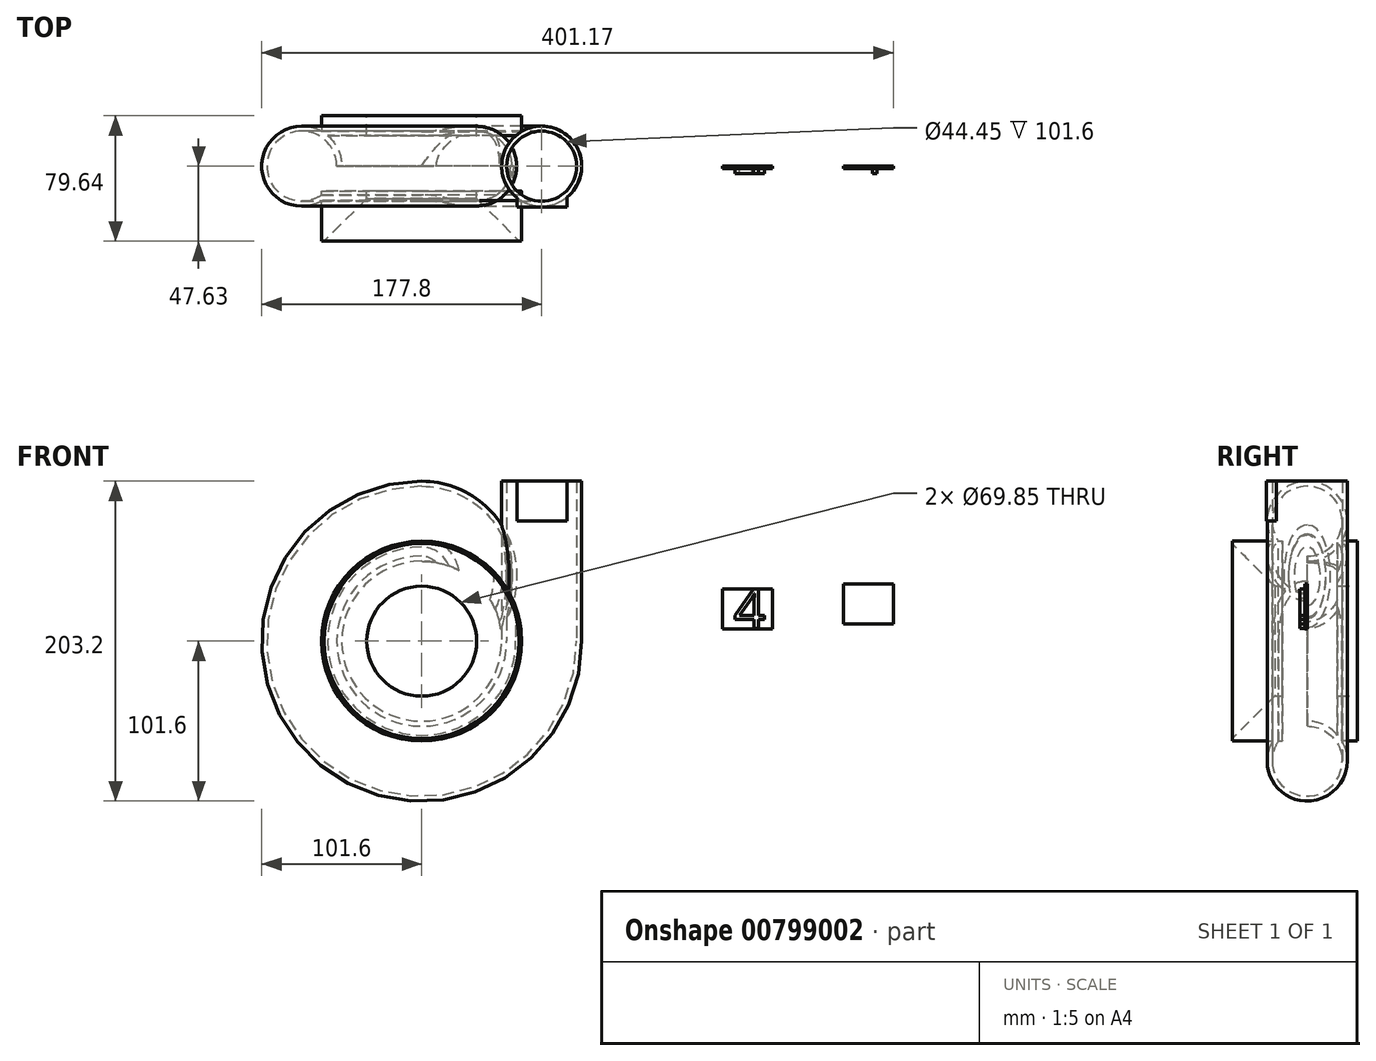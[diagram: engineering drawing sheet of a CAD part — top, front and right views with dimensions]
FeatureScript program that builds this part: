
annotation { "Feature Type Name" : "Feature", "Feature Type Description" : "" }
export const myFeature = defineFeature(function(context is Context, id is Id, definition is map)
    precondition{}
    {
        {
            var Q0;
            Q0=qCreatedBy(makeId("Front.planeOp"),FACE);
            var sketch = newSketch(context, id + "F0", { "sketchPlane" : qUnion([Q0])});
            skCircle(sketch, "E0", {"center": v(0, 0) * mm, "radius": 38.1 * mm});
            skCircle(sketch, "E1", {"center": v(0, 0) * mm, "radius": 50.8 * mm});
            skLineSegment(sketch, "E2.bottom", {"start": v(222.87, 7.67) * mm, "end": v(191.12, 7.67) * mm});
            skLineSegment(sketch, "E2.top", {"start": v(222.87, 33.07) * mm, "end": v(191.12, 33.07) * mm});
            skLineSegment(sketch, "E2.left", {"start": v(222.87, 7.67) * mm, "end": v(222.87, 33.07) * mm});
            skLineSegment(sketch, "E2.right", {"start": v(191.12, 7.67) * mm, "end": v(191.12, 33.07) * mm});
            skPoint(sketch, "E2.middle", {"position": v(207, 20.37) * mm});
            skLineSegment(sketch, "E3.bottom", {"start": v(299.57, 11.1) * mm, "end": v(267.82, 11.1) * mm});
            skLineSegment(sketch, "E3.top", {"start": v(299.57, 36.5) * mm, "end": v(267.82, 36.5) * mm});
            skLineSegment(sketch, "E3.left", {"start": v(299.57, 11.1) * mm, "end": v(299.57, 36.5) * mm});
            skLineSegment(sketch, "E3.right", {"start": v(267.82, 11.1) * mm, "end": v(267.82, 36.5) * mm});
            skPoint(sketch, "E3.middle", {"position": v(283.7, 23.8) * mm});
            skSolve(sketch);
        }
        {
            var Q0;
            Q0=qCreatedBy(makeId("Right.planeOp"),FACE);
            var sketch = newSketch(context, id + "F1", { "sketchPlane" : qUnion([Q0])});
            skCircle(sketch, "E4", {"center": v(0, 76.2) * mm, "radius": 25.4 * mm});
            skCircle(sketch, "E5", {"center": v(0, 76.2) * mm, "radius": 22.23 * mm});
            skSolve(sketch);
        }
        {
            var Q0;
            Q0=makeQuery(id+"F1.imprint","IMPRINT",FACE,{"disambiguationData":[TD([[makeQuery(id+"F1.imprint","IMPRINT",EDGE,{"derivedFrom":sQuery(id+"F1.wireOp",EDGE,"E4")}),1.0]])]});
            var Q1;
            Q1=sQuery(id+"F0.wireOp",EDGE,"E1");
            revolve(context, id + "F2", {"surfaceOperationType" : NewSurfaceOperationType.NEW, "entities" : qUnion([Q0]), "axis" : qUnion([Q1]), "revolveType" : RevolveType.ONE_DIRECTION, "angle" : 270 * degree});
        }
        {
            var Q0;
            Q0=makeQuery(id+"F2.opRevolve","CAP_FACE",FACE,{"disambiguationData":[OSD([sQuery(id+"F1.wireOp",EDGE,"E4"),sQuery(id+"F1.wireOp",EDGE,"E5")])],"isStart":false});
            extrude(context, id + "F3", {"entities" : qUnion([Q0]), "operationType" : NewBodyOperationType.ADD, "depth" : 101.6 * mm, "offsetDistance" : 25.4 * mm});
        }
        {
            var Q0;
            Q0=qCreatedBy(makeId("Front.planeOp"),FACE);
            var sketch = newSketch(context, id + "F4", { "sketchPlane" : qUnion([Q0])});
            skCircle(sketch, "E6", {"center": v(0, 41.28) * mm, "radius": 9.53 * mm, "construction": true});
            skSolve(sketch);
        }
        {
            var Q0;
            Q0=makeQuery(id+"F1.imprint","IMPRINT",FACE,{"disambiguationData":[TD([[makeQuery(id+"F1.imprint","IMPRINT",EDGE,{"derivedFrom":sQuery(id+"F1.wireOp",EDGE,"E4")}),1.0]])]});
            var Q1;
            Q1=sQuery(id+"F4.wireOp",EDGE,"E6");
            revolve(context, id + "F5", {"operationType" : NewBodyOperationType.ADD, "surfaceOperationType" : NewSurfaceOperationType.NEW, "entities" : qUnion([Q0]), "axis" : qUnion([Q1]), "revolveType" : RevolveType.ONE_DIRECTION, "oppositeDirection" : true, "angle" : 129.12 * degree});
        }
        {
            var Q0;
            Q0=sQuery(id+"F0.wireOp",VERTEX,"E1.center");
            var Q1;
            Q1=makeQuery(id+"F2.opRevolve","SWEPT_BODY",BODY,{"disambiguationData":[OSD([sQuery(id+"F1.wireOp",EDGE,"E4"),sQuery(id+"F1.wireOp",EDGE,"E5")])]});
            hole(context, id + "F6", {"style" : HoleStyle.SIMPLE, "endStyle" : HoleEndStyle.THROUGH, "holeDiameter" : 101.6 * mm, "majorDiameter" : 6.35 * mm, "isTappedThrough" : true, "tappedDepth" : 12.7 * mm, "tapClearance" : 3, "locations" : qUnion([Q0]), "scope" : qUnion([Q1]), "startStyle" : HoleStartStyle.PART});
        }
        {
            var Q0;
            Q0=sQuery(id+"F0.wireOp",VERTEX,"E1.center");
            var Q1;
            Q1=makeQuery(id+"F2.opRevolve","SWEPT_BODY",BODY,{"disambiguationData":[OSD([sQuery(id+"F1.wireOp",EDGE,"E4"),sQuery(id+"F1.wireOp",EDGE,"E5")])]});
            hole(context, id + "F7", {"style" : HoleStyle.SIMPLE, "endStyle" : HoleEndStyle.THROUGH, "oppositeDirection" : true, "holeDiameter" : 127 * mm, "majorDiameter" : 6.35 * mm, "isTappedThrough" : true, "tappedDepth" : 12.7 * mm, "tapClearance" : 3, "locations" : qUnion([Q0]), "scope" : qUnion([Q1]), "startStyle" : HoleStartStyle.PART});
        }
        {
            var Q0;
            Q0=makeQuery(id+"F0.imprint","IMPRINT",FACE,{"disambiguationData":[TD([[makeQuery(id+"F0.imprint","IMPRINT",EDGE,{"derivedFrom":sQuery(id+"F0.wireOp",EDGE,"E0")}),1.0]])]});
            cPlane(context, id + "F8", {"entities" : qUnion([Q0]), "cplaneType" : CPlaneType.OFFSET, "offset" : 15.88 * mm, "width" : 152.4 * mm, "height" : 152.4 * mm});
        }
        {
            var Q0;
            Q0=qCreatedBy(id+"F8.planeOp",FACE);
            var sketch = newSketch(context, id + "F9", { "sketchPlane" : qUnion([Q0])});
            skCircle(sketch, "E7", {"center": v(0, 0) * mm, "radius": 63.5 * mm});
            skSolve(sketch);
        }
        {
            var Q0;
            Q0=makeQuery(id+"F9.imprint","IMPRINT",FACE,{"disambiguationData":[TD([[makeQuery(id+"F9.imprint","IMPRINT",EDGE,{"derivedFrom":sQuery(id+"F9.wireOp",EDGE,"E7")}),1.0]])]});
            extrude(context, id + "F10", {"entities" : qUnion([Q0]), "operationType" : NewBodyOperationType.ADD, "depth" : 31.75 * mm, "offsetDistance" : 25.4 * mm});
        }
        {
            var Q0;
            Q0=makeQuery(id+"F0.imprint","IMPRINT",FACE,{"disambiguationData":[TD([[makeQuery(id+"F0.imprint","IMPRINT",EDGE,{"derivedFrom":sQuery(id+"F0.wireOp",EDGE,"E0")}),-1.0]])]});
            cPlane(context, id + "F11", {"entities" : qUnion([Q0]), "cplaneType" : CPlaneType.OFFSET, "offset" : 19.3 * mm, "oppositeDirection" : true, "width" : 152.4 * mm, "height" : 152.4 * mm});
        }
        {
            var Q0;
            Q0=qCreatedBy(id+"F11.planeOp",FACE);
            var sketch = newSketch(context, id + "F12", { "sketchPlane" : qUnion([Q0])});
            skCircle(sketch, "E8", {"center": v(0, 0) * mm, "radius": 63.5 * mm});
            skSolve(sketch);
        }
        {
            var Q0;
            Q0=makeQuery(id+"F12.imprint","IMPRINT",FACE,{"disambiguationData":[TD([[makeQuery(id+"F12.imprint","IMPRINT",EDGE,{"derivedFrom":sQuery(id+"F12.wireOp",EDGE,"E8")}),1.0]])]});
            extrude(context, id + "F13", {"entities" : qUnion([Q0]), "operationType" : NewBodyOperationType.ADD, "oppositeDirection" : true, "depth" : 12.7 * mm, "offsetDistance" : 25.4 * mm});
        }
        {
            var Q0;
            Q0=makeQuery(id+"F10.opExtrude","CAP_FACE",FACE,{"disambiguationData":[OSD([sQuery(id+"F9.wireOp",EDGE,"E7")])],"isStart":false});
            var sketch = newSketch(context, id + "F14", { "sketchPlane" : qUnion([Q0])});
            skPoint(sketch, "E9", {"position": v(0, 0) * mm});
            skSolve(sketch);
        }
        {
            var Q0;
            Q0=sQuery(id+"F14.wireOp",VERTEX,"E9");
            var Q1;
            Q1=makeQuery(id+"F2.opRevolve","SWEPT_BODY",BODY,{"disambiguationData":[OSD([sQuery(id+"F1.wireOp",EDGE,"E4"),sQuery(id+"F1.wireOp",EDGE,"E5")])]});
            hole(context, id + "F15", {"style" : HoleStyle.C_SINK, "endStyle" : HoleEndStyle.THROUGH, "holeDiameter" : 69.85 * mm, "cSinkDiameter" : 123.82 * mm, "cSinkAngle" : 90 * degree, "majorDiameter" : 6.35 * mm, "isTappedThrough" : true, "tappedDepth" : 12.7 * mm, "tapClearance" : 3, "locations" : qUnion([Q0]), "scope" : qUnion([Q1]), "startStyle" : HoleStartStyle.PART});
        }
        {
            var Q0;
            Q0=makeQuery(id+"F3.opExtrude","CAP_FACE",FACE,{"disambiguationData":[OSD([sQuery(id+"F1.wireOp",EDGE,"E4"),sQuery(id+"F1.wireOp",EDGE,"E5")])],"isStart":false});
            cPlane(context, id + "F16", {"entities" : qUnion([Q0]), "cplaneType" : CPlaneType.OFFSET, "offset" : 0 * mm, "width" : 152.4 * mm, "height" : 152.4 * mm});
        }
        {
            var Q0;
            Q0=qCreatedBy(id+"F16.planeOp",FACE);
            var sketch = newSketch(context, id + "F17", { "sketchPlane" : qUnion([Q0])});
            skLineSegment(sketch, "E10.bottom", {"start": v(92.23, -25.89) * mm, "end": v(60.48, -25.89) * mm});
            skLineSegment(sketch, "E10.top", {"start": v(92.23, -18.32) * mm, "end": v(60.48, -18.32) * mm});
            skLineSegment(sketch, "E10.left", {"start": v(92.23, -25.89) * mm, "end": v(92.23, -18.32) * mm});
            skLineSegment(sketch, "E10.right", {"start": v(60.48, -25.89) * mm, "end": v(60.48, -18.32) * mm});
            skPoint(sketch, "E10.middle", {"position": v(76.36, -22.1) * mm});
            skCircle(sketch, "E11", {"center": v(76.09, -0.08) * mm, "radius": 25.25 * mm});
            skSolve(sketch);
        }
        {
            var Q0;
            {var subQ0=sQuery(id+"F17.wireOp",EDGE,"E10.bottom");Q0=makeQuery(id+"F17.imprint","IMPRINT",FACE,{"disambiguationData":[TD([[makeQuery(id+"F17.imprint","IMPRINT",EDGE,{"derivedFrom":subQ0}),-1.0]])]});}
            extrude(context, id + "F18", {"entities" : qUnion([Q0]), "operationType" : NewBodyOperationType.ADD, "oppositeDirection" : true, "depth" : 25.4 * mm, "offsetDistance" : 25.4 * mm});
        }
        {
            var Q0;
            Q0=makeQuery(id+"F0.imprint","IMPRINT",FACE,{"disambiguationData":[TD([[makeQuery(id+"F0.imprint","IMPRINT",EDGE,{"derivedFrom":sQuery(id+"F0.wireOp",EDGE,"E2.bottom")}),-1.0]])]});
            extrude(context, id + "F19", {"entities" : qUnion([Q0]), "depth" : 1.59 * mm, "offsetDistance" : 25.4 * mm});
        }
        {
            var Q0;
            Q0=makeQuery(id+"F0.imprint","IMPRINT",FACE,{"disambiguationData":[TD([[makeQuery(id+"F0.imprint","IMPRINT",EDGE,{"derivedFrom":sQuery(id+"F0.wireOp",EDGE,"E3.bottom")}),-1.0]])]});
            extrude(context, id + "F20", {"entities" : qUnion([Q0]), "depth" : 1.59 * mm, "offsetDistance" : 25.4 * mm});
        }
        {
            var Q0;
            Q0=makeQuery(id+"F20.opExtrude","CAP_FACE",FACE,{"disambiguationData":[OSD([sQuery(id+"F0.wireOp",EDGE,"E3.bottom"),sQuery(id+"F0.wireOp",EDGE,"E3.top"),sQuery(id+"F0.wireOp",EDGE,"E3.left"),sQuery(id+"F0.wireOp",EDGE,"E3.right")])],"isStart":false});
            var sketch = newSketch(context, id + "F21", { "sketchPlane" : qUnion([Q0])});
            skText(sketch, "E12", { "text": "1\n", "fontName": "OpenSans-Regular.ttf"});
            skText(sketch, "E13", { "text": "4", "fontName": "OpenSans-Regular.ttf"});
            const initialGuessF21  = {"E12": [0.2749, 0.0111, 1, 0, 0.0254], "E13": [0.19827, 0.00806, 1, 0, 0.02516]};
            skSetInitialGuess(sketch, initialGuessF21);
            skSolve(sketch);
        }
        {
            var Q0;
            Q0=makeQuery(id+"F21.imprint","IMPRINT",FACE,{"disambiguationData":[TD([[makeQuery(id+"F21.imprint","IMPRINT",EDGE,{"derivedFrom":sQuery(id+"F21.wireOp",EDGE,"E13.sketch_text.stroke-0")}),-1.0]])]});
            extrude(context, id + "F22", {"entities" : qUnion([Q0]), "operationType" : NewBodyOperationType.ADD, "depth" : 3.17 * mm, "offsetDistance" : 25.4 * mm});
        }
        {
            var Q0;
            Q0=makeQuery(id+"F20.opExtrude","CAP_FACE",FACE,{"disambiguationData":[OSD([sQuery(id+"F0.wireOp",EDGE,"E3.bottom"),sQuery(id+"F0.wireOp",EDGE,"E3.top"),sQuery(id+"F0.wireOp",EDGE,"E3.left"),sQuery(id+"F0.wireOp",EDGE,"E3.right")])],"isStart":false});
            var sketch = newSketch(context, id + "F23", { "sketchPlane" : qUnion([Q0])});
            skText(sketch, "E14", { "text": "1", "fontName": "OpenSans-Regular.ttf"});
            const initialGuessF23  = {"E14": [0.2767, 0.0111, 1, 0, 0.0254]};
            skSetInitialGuess(sketch, initialGuessF23);
            skSolve(sketch);
        }
        {
            var Q0;
            Q0=makeQuery(id+"F23.imprint","IMPRINT",FACE,{"disambiguationData":[TD([[makeQuery(id+"F23.imprint","IMPRINT",EDGE,{"derivedFrom":sQuery(id+"F23.wireOp",EDGE,"E14.sketch_text.stroke-0")}),-1.0]])]});
            extrude(context, id + "F24", {"entities" : qUnion([Q0]), "operationType" : NewBodyOperationType.ADD, "depth" : 3.17 * mm, "offsetDistance" : 25.4 * mm});
        }
    });
